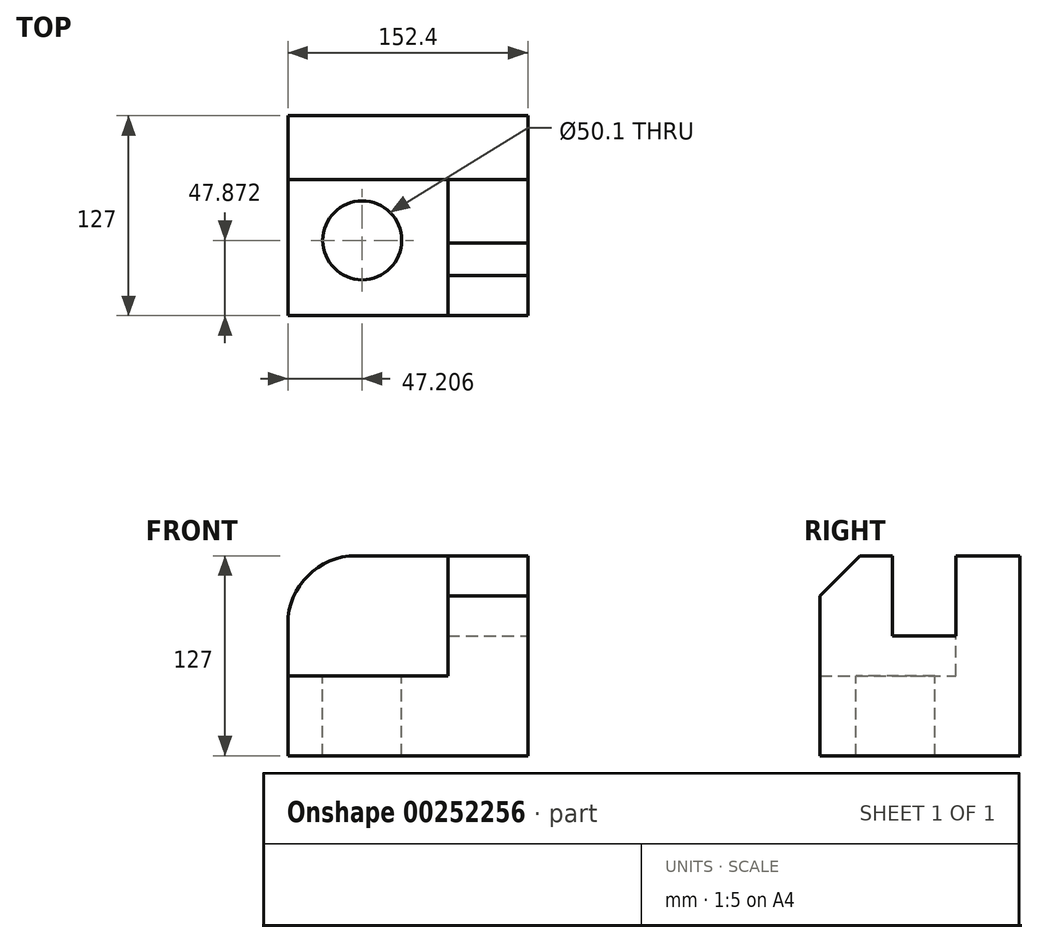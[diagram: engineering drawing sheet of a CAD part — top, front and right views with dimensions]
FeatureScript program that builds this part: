
annotation { "Feature Type Name" : "Feature", "Feature Type Description" : "" }
export const myFeature = defineFeature(function(context is Context, id is Id, definition is map)
    precondition{}
    {
        {
            var Q0;
            Q0=qCreatedBy(makeId("Front.planeOp"),FACE);
            var sketch = newSketch(context, id + "F0", { "sketchPlane" : qUnion([Q0])});
            skLineSegment(sketch, "E0.bottom", {"start": v(-76.2, 63.5) * mm, "end": v(76.2, 63.5) * mm});
            skLineSegment(sketch, "E0.top", {"start": v(-76.2, -63.5) * mm, "end": v(76.2, -63.5) * mm});
            skLineSegment(sketch, "E0.left", {"start": v(-76.2, 63.5) * mm, "end": v(-76.2, -63.5) * mm});
            skLineSegment(sketch, "E0.right", {"start": v(76.2, 63.5) * mm, "end": v(76.2, -63.5) * mm});
            skPoint(sketch, "E0.middle", {"position": v(0, 0) * mm});
            skSolve(sketch);
        }
        {
            var Q0;
            Q0=makeQuery(id+"F0.imprint","IMPRINT",FACE,{"disambiguationData":[TD([[makeQuery(id+"F0.imprint","IMPRINT",EDGE,{"derivedFrom":sQuery(id+"F0.wireOp",EDGE,"E0.bottom")}),-1.0]])]});
            extrude(context, id + "F1", {"entities" : qUnion([Q0]), "endBound" : BoundingType.SYMMETRIC, "depth" : 127 * mm});
        }
        {
            var Q0;
            Q0=makeQuery(id+"F1.opExtrude","SWEPT_FACE",FACE,{"disambiguationData":[OSD([sQuery(id+"F0.wireOp",EDGE,"E0.bottom")])]});
            var sketch = newSketch(context, id + "F2", { "sketchPlane" : qUnion([Q0])});
            skLineSegment(sketch, "E1", {"start": v(25.4, -63.5) * mm, "end": v(25.4, 22.82) * mm});
            skLineSegment(sketch, "E2", {"start": v(25.4, 22.82) * mm, "end": v(-76.2, 22.82) * mm});
            skLineSegment(sketch, "E3", {"start": v(-76.2, 22.82) * mm, "end": v(-76.2, -63.5) * mm});
            skLineSegment(sketch, "E4", {"start": v(-76.2, -63.5) * mm, "end": v(25.4, -63.5) * mm});
            skSolve(sketch);
        }
        {
            var Q0;
            Q0=makeQuery(id+"F2.imprint","IMPRINT",FACE,{"disambiguationData":[TD([[makeQuery(id+"F2.imprint","IMPRINT",EDGE,{"derivedFrom":sQuery(id+"F2.wireOp",EDGE,"E1")}),1.0]])]});
            extrude(context, id + "F3", {"entities" : qUnion([Q0]), "operationType" : NewBodyOperationType.REMOVE, "oppositeDirection" : true, "depth" : 76.2 * mm});
        }
        {
            var Q0;
            Q0=makeQuery(id+"F1.opExtrude","SWEPT_FACE",FACE,{"disambiguationData":[OSD([sQuery(id+"F0.wireOp",EDGE,"E0.bottom")])]});
            var sketch = newSketch(context, id + "F4", { "sketchPlane" : qUnion([Q0])});
            skLineSegment(sketch, "E5", {"start": v(25.4, 22.82) * mm, "end": v(76.2, 22.82) * mm});
            skLineSegment(sketch, "E6", {"start": v(76.2, 22.82) * mm, "end": v(76.2, -17.33) * mm});
            skLineSegment(sketch, "E7", {"start": v(76.2, -17.33) * mm, "end": v(25.4, -17.33) * mm});
            skLineSegment(sketch, "E8", {"start": v(25.4, -17.33) * mm, "end": v(25.4, 22.82) * mm});
            skSolve(sketch);
        }
        {
            var Q0;
            Q0=makeQuery(id+"F4.imprint","IMPRINT",FACE,{"disambiguationData":[TD([[makeQuery(id+"F4.imprint","IMPRINT",EDGE,{"derivedFrom":sQuery(id+"F4.wireOp",EDGE,"E5")}),-1.0]])]});
            var Q1;
            Q1=sQuery(id+"F4.wireOp",EDGE,"E5");
            var Q2;
            Q2=sQuery(id+"F4.wireOp",EDGE,"E6");
            var Q3;
            Q3=sQuery(id+"F4.wireOp",EDGE,"E7");
            var Q4;
            Q4=sQuery(id+"F4.wireOp",EDGE,"E8");
            extrude(context, id + "F5", {"entities" : qUnion([Q0]), "operationType" : NewBodyOperationType.REMOVE, "surfaceEntities" : qUnion([Q1, Q2, Q3, Q4]), "oppositeDirection" : true, "depth" : 50.8 * mm});
        }
        {
            var Q0;
            Q0=makeQuery(id+"F1.opExtrude","CAP_EDGE",EDGE,{"disambiguationData":[OSD([sQuery(id+"F0.wireOp",EDGE,"E0.bottom")])],"isStart":false});
            chamfer(context, id + "F6", {"entities" : qUnion([Q0]), "width" : 25.4 * mm, "tangentPropagation" : true});
        }
        {
            var Q0;
            Q0=makeQuery(id+"F1.opExtrude","SWEPT_EDGE",EDGE,{"disambiguationData":[OSD([sQuery(id+"F0.wireOp",EDGE,"E0.bottom"),sQuery(id+"F0.wireOp",EDGE,"E0.left")])]});
            fillet(context, id + "F7", {"entities" : qUnion([Q0]), "radius" : 43.18 * mm, "tangentPropagation" : true, "allowEdgeOverflow" : false});
        }
        {
            var Q0;
            Q0=makeQuery(id+"F3.boolean.opBoolean","COPY",FACE,{"derivedFrom":makeQuery(id+"F3.opExtrude","CAP_FACE",FACE,{"disambiguationData":[OSD([sQuery(id+"F2.wireOp",EDGE,"E1"),sQuery(id+"F2.wireOp",EDGE,"E2"),sQuery(id+"F2.wireOp",EDGE,"E3"),sQuery(id+"F2.wireOp",EDGE,"E4")])],"isStart":false})});
            var sketch = newSketch(context, id + "F8", { "sketchPlane" : qUnion([Q0])});
            skCircle(sketch, "E9", {"center": v(-29, -15.63) * mm, "radius": 25.05 * mm});
            skSolve(sketch);
        }
        {
            var Q0;
            Q0=makeQuery(id+"F8.imprint","IMPRINT",FACE,{"disambiguationData":[TD([[makeQuery(id+"F8.imprint","IMPRINT",EDGE,{"derivedFrom":sQuery(id+"F8.wireOp",EDGE,"E9")}),1.0]])]});
            var Q1;
            Q1=makeQuery(id+"F1.opExtrude","SWEPT_FACE",FACE,{"disambiguationData":[OSD([sQuery(id+"F0.wireOp",EDGE,"E0.top")])]});
            extrude(context, id + "F9", {"entities" : qUnion([Q0]), "operationType" : NewBodyOperationType.REMOVE, "endBound" : BoundingType.UP_TO_SURFACE, "oppositeDirection" : true, "endBoundEntityFace" : qUnion([Q1]), "depth" : 25.4 * mm});
        }
    });
